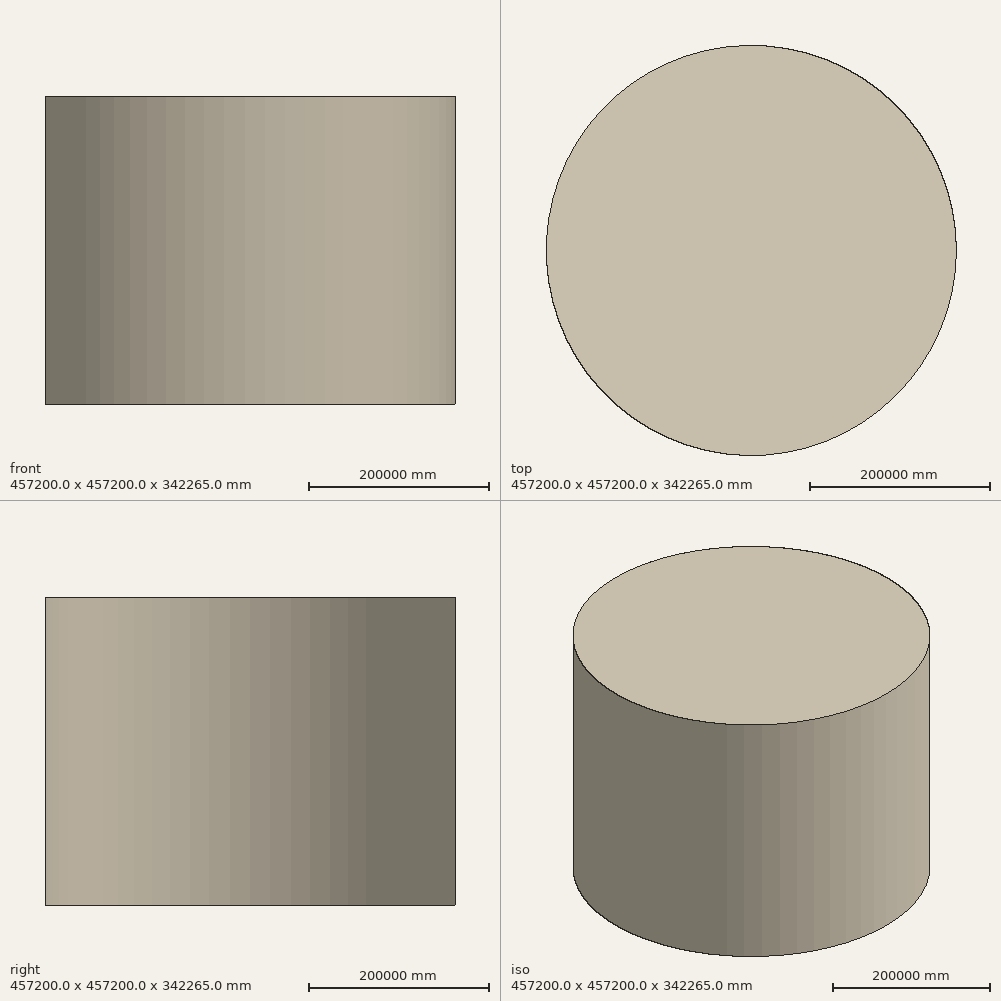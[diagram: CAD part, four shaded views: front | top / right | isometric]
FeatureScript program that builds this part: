
annotation { "Feature Type Name" : "Feature", "Feature Type Description" : "" }
export const myFeature = defineFeature(function(context is Context, id is Id, definition is map)
    precondition{}
    {
        {
            var Q0;
            Q0=qCreatedBy(makeId("Top.planeOp"),FACE);
            var sketch = newSketch(context, id + "F0", { "sketchPlane" : qUnion([Q0])});
            skCircle(sketch, "E0", {"center": v(0, 0) * mm, "radius": 228600 * mm});
            skSolve(sketch);
        }
        {
            var Q0;
            Q0=makeQuery(id+"F0.imprint","IMPRINT",FACE,{"disambiguationData":[TD([[makeQuery(id+"F0.imprint","IMPRINT",EDGE,{"derivedFrom":sQuery(id+"F0.wireOp",EDGE,"E0")}),1.0]])]});
            extrude(context, id + "F1", {"entities" : qUnion([Q0]), "depth" : 342265 * mm, "offsetDistance" : 25.4 * mm});
        }
    });
